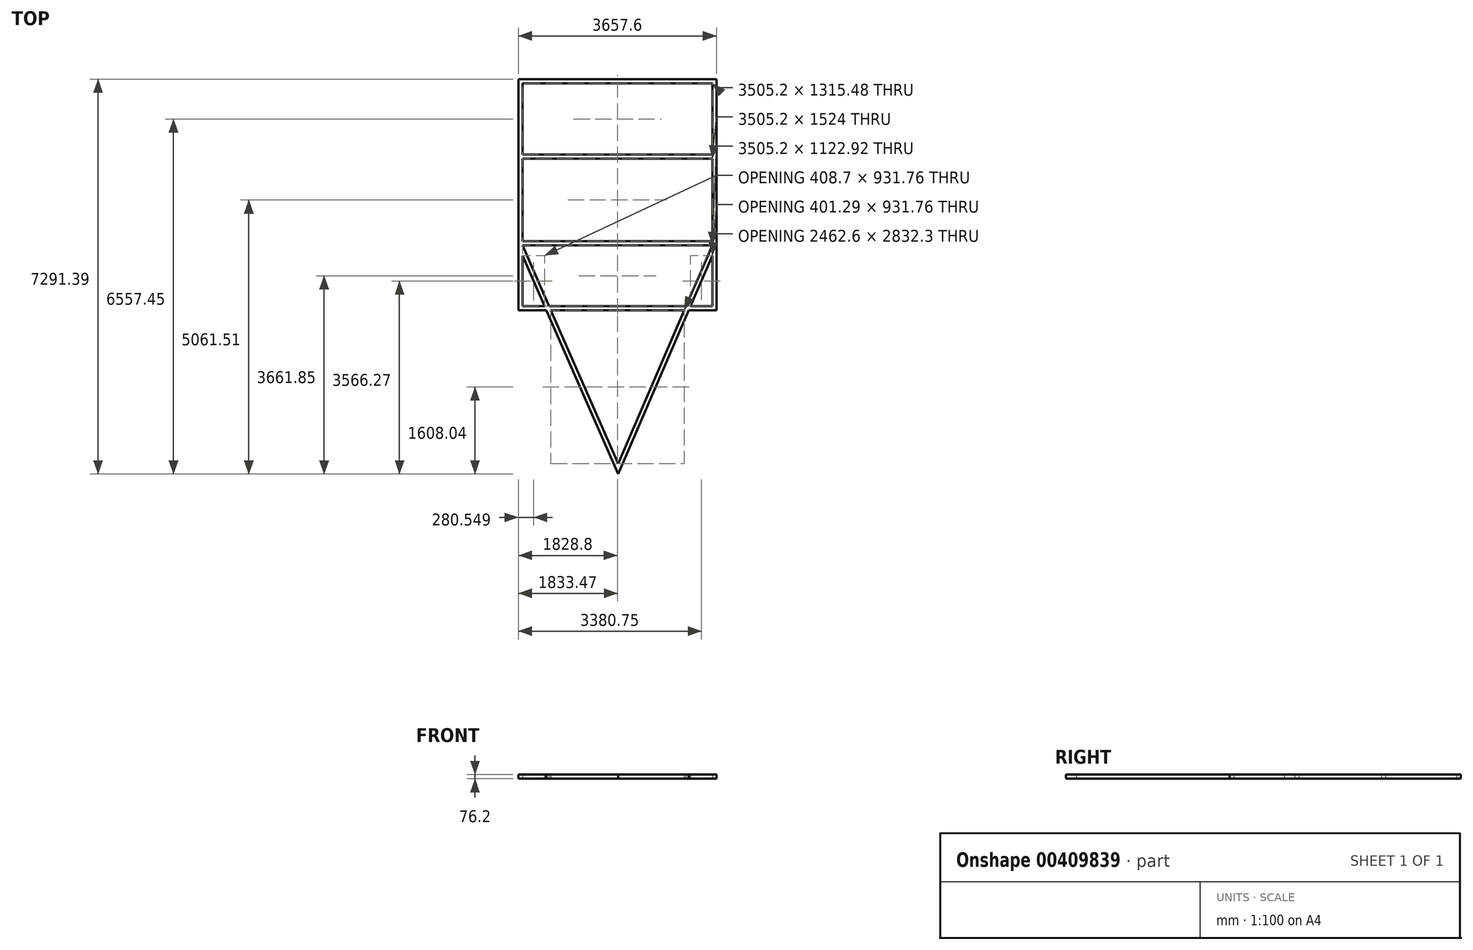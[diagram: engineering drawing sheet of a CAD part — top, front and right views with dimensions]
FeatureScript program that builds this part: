
annotation { "Feature Type Name" : "Feature", "Feature Type Description" : "" }
export const myFeature = defineFeature(function(context is Context, id is Id, definition is map)
    precondition{}
    {
        {
            var Q0;
            Q0=qCreatedBy(makeId("Top.planeOp"),FACE);
            var sketch = newSketch(context, id + "F0", { "sketchPlane" : qUnion([Q0])});
            skLineSegment(sketch, "E0.bottom", {"start": v(1828.8, 2133.6) * mm, "end": v(-1828.8, 2133.6) * mm});
            skLineSegment(sketch, "E0.top", {"start": v(1828.8, -2133.6) * mm, "end": v(-1828.8, -2133.6) * mm});
            skLineSegment(sketch, "E0.left", {"start": v(1828.8, 2133.6) * mm, "end": v(1828.8, -2133.6) * mm});
            skLineSegment(sketch, "E0.right", {"start": v(-1828.8, 2133.6) * mm, "end": v(-1828.8, -2133.6) * mm});
            skLineSegment(sketch, "E1.bottom", {"start": v(1752.6, -2057.4) * mm, "end": v(-1752.6, -2057.4) * mm});
            skLineSegment(sketch, "E1.top", {"start": v(1752.6, 2057.4) * mm, "end": v(-1752.6, 2057.4) * mm});
            skLineSegment(sketch, "E1.left", {"start": v(1752.6, -2057.4) * mm, "end": v(1752.6, 2057.4) * mm});
            skLineSegment(sketch, "E1.right", {"start": v(-1752.6, -2057.4) * mm, "end": v(-1752.6, 2057.4) * mm});
            skPoint(sketch, "E1.middle", {"position": v(0, 0) * mm});
            skPoint(sketch, "E2", {"position": v(0, -2133.6) * mm});
            skLineSegment(sketch, "E3", {"start": v(15.7, -4965.9) * mm, "end": v(1752.6, -934.48) * mm});
            skLineSegment(sketch, "E4", {"start": v(1752.6, -934.48) * mm, "end": v(-1752.6, -934.48) * mm});
            skLineSegment(sketch, "E5", {"start": v(-1752.6, -934.48) * mm, "end": v(15.7, -4965.9) * mm});
            skLineSegment(sketch, "E6", {"start": v(1752.6, -1125.64) * mm, "end": v(16.03, -5157.8) * mm});
            skLineSegment(sketch, "E7", {"start": v(16.03, -5157.8) * mm, "end": v(-1752.6, -1125.64) * mm});
            skLineSegment(sketch, "E8", {"start": v(-1752.6, -858.28) * mm, "end": v(1752.6, -858.28) * mm});
            skLineSegment(sketch, "E9", {"start": v(-1752.6, -1125.64) * mm, "end": v(-1752.6, -858.28) * mm});
            skLineSegment(sketch, "E10", {"start": v(1752.6, -858.28) * mm, "end": v(1752.6, -1125.64) * mm});
            skLineSegment(sketch, "E11.bottom", {"start": v(-1752.6, 665.72) * mm, "end": v(1752.6, 665.72) * mm});
            skLineSegment(sketch, "E11.top", {"start": v(-1752.6, 741.92) * mm, "end": v(1752.6, 741.92) * mm});
            skLineSegment(sketch, "E11.left", {"start": v(-1752.6, 665.72) * mm, "end": v(-1752.6, 741.92) * mm});
            skLineSegment(sketch, "E11.right", {"start": v(1752.6, 665.72) * mm, "end": v(1752.6, 741.92) * mm});
            skPoint(sketch, "E12.middle", {"position": v(16.03, -5157.8) * mm});
            skPoint(sketch, "E13.endSnap0", {"position": v(0, 665.72) * mm});
            skSolve(sketch);
        }
        {
            var Q0;
            Q0=makeQuery(id+"F0.imprint","IMPRINT",FACE,{"disambiguationData":[TD([[makeQuery(id+"F0.imprint","IMPRINT",EDGE,{"derivedFrom":sQuery(id+"F0.wireOp",EDGE,"E0.bottom")}),1.0]])]});
            extrude(context, id + "F1", {"entities" : qUnion([Q0]), "depth" : 76.2 * mm});
        }
        {
            var Q0;
            {var subQ3=sQuery(id+"F0.wireOp",EDGE,"E0.top");var subQ6=sQuery(id+"F0.wireOp",EDGE,"E6");var subQ7=makeQuery(id+"F0.imprint","INTERSECT",VERTEX,{"derivedFrom":[subQ3,subQ6]});Q0=makeQuery(id+"F0.imprint","IMPRINT",FACE,{"disambiguationData":[TD([[makeQuery(id+"F0.imprint","IMPRINT",EDGE,{"disambiguationData":[TD([[subQ7,-1.0]])],"derivedFrom":subQ3}),1.0]])]});}
            var Q1;
            {var subQ0=sQuery(id+"F0.wireOp",EDGE,"E7");var subQ1=sQuery(id+"F0.wireOp",EDGE,"E0.top");var subQ2=makeQuery(id+"F0.imprint","INTERSECT",VERTEX,{"derivedFrom":[subQ1,subQ0]});Q1=makeQuery(id+"F0.imprint","IMPRINT",FACE,{"disambiguationData":[TD([[makeQuery(id+"F0.imprint","IMPRINT",EDGE,{"disambiguationData":[TD([[subQ2,1.0]])],"derivedFrom":subQ1}),-1.0]])]});}
            var Q2;
            {var subQ0=sQuery(id+"F0.wireOp",EDGE,"E5");var subQ1=sQuery(id+"F0.wireOp",EDGE,"E1.bottom");var subQ2=makeQuery(id+"F0.imprint","INTERSECT",VERTEX,{"derivedFrom":[subQ1,subQ0]});Q2=makeQuery(id+"F0.imprint","IMPRINT",FACE,{"disambiguationData":[TD([[makeQuery(id+"F0.imprint","IMPRINT",EDGE,{"disambiguationData":[TD([[subQ2,-1.0]])],"derivedFrom":subQ1}),-1.0]])]});}
            var Q3;
            {var subQ0=sQuery(id+"F0.wireOp",EDGE,"E3");var subQ1=sQuery(id+"F0.wireOp",EDGE,"E0.top");var subQ2=makeQuery(id+"F0.imprint","INTERSECT",VERTEX,{"derivedFrom":[subQ1,subQ0]});Q3=makeQuery(id+"F0.imprint","IMPRINT",FACE,{"disambiguationData":[TD([[makeQuery(id+"F0.imprint","IMPRINT",EDGE,{"disambiguationData":[TD([[subQ2,-1.0]])],"derivedFrom":subQ1}),-1.0]])]});}
            var Q4;
            {var subQ0=sQuery(id+"F0.wireOp",EDGE,"E6");var subQ1=sQuery(id+"F0.wireOp",EDGE,"E0.top");var subQ2=makeQuery(id+"F0.imprint","INTERSECT",VERTEX,{"derivedFrom":[subQ1,subQ0]});Q4=makeQuery(id+"F0.imprint","IMPRINT",FACE,{"disambiguationData":[TD([[makeQuery(id+"F0.imprint","IMPRINT",EDGE,{"disambiguationData":[TD([[subQ2,-1.0]])],"derivedFrom":subQ1}),-1.0]])]});}
            var Q5;
            {var subQ0=sQuery(id+"F0.wireOp",EDGE,"E6");var subQ1=sQuery(id+"F0.wireOp",EDGE,"E1.bottom");var subQ2=makeQuery(id+"F0.imprint","INTERSECT",VERTEX,{"derivedFrom":[subQ1,subQ0]});Q5=makeQuery(id+"F0.imprint","IMPRINT",FACE,{"disambiguationData":[TD([[makeQuery(id+"F0.imprint","IMPRINT",EDGE,{"disambiguationData":[TD([[subQ2,-1.0]])],"derivedFrom":subQ1}),-1.0]])]});}
            var Q6;
            {var subQ0=sQuery(id+"F0.wireOp",EDGE,"E4");Q6=makeQuery(id+"F0.imprint","IMPRINT",FACE,{"disambiguationData":[TD([[makeQuery(id+"F0.imprint","IMPRINT",EDGE,{"derivedFrom":subQ0}),-1.0]])]});}
            extrude(context, id + "F2", {"entities" : qUnion([Q0, Q1, Q2, Q3, Q4, Q5, Q6]), "operationType" : NewBodyOperationType.ADD, "depth" : 76.2 * mm});
        }
        {
            var Q0;
            Q0=makeQuery(id+"F0.imprint","IMPRINT",FACE,{"disambiguationData":[TD([[makeQuery(id+"F0.imprint","IMPRINT",EDGE,{"derivedFrom":sQuery(id+"F0.wireOp",EDGE,"E11.bottom")}),1.0]])]});
            extrude(context, id + "F3", {"entities" : qUnion([Q0]), "operationType" : NewBodyOperationType.ADD, "depth" : 76.2 * mm});
        }
    });
